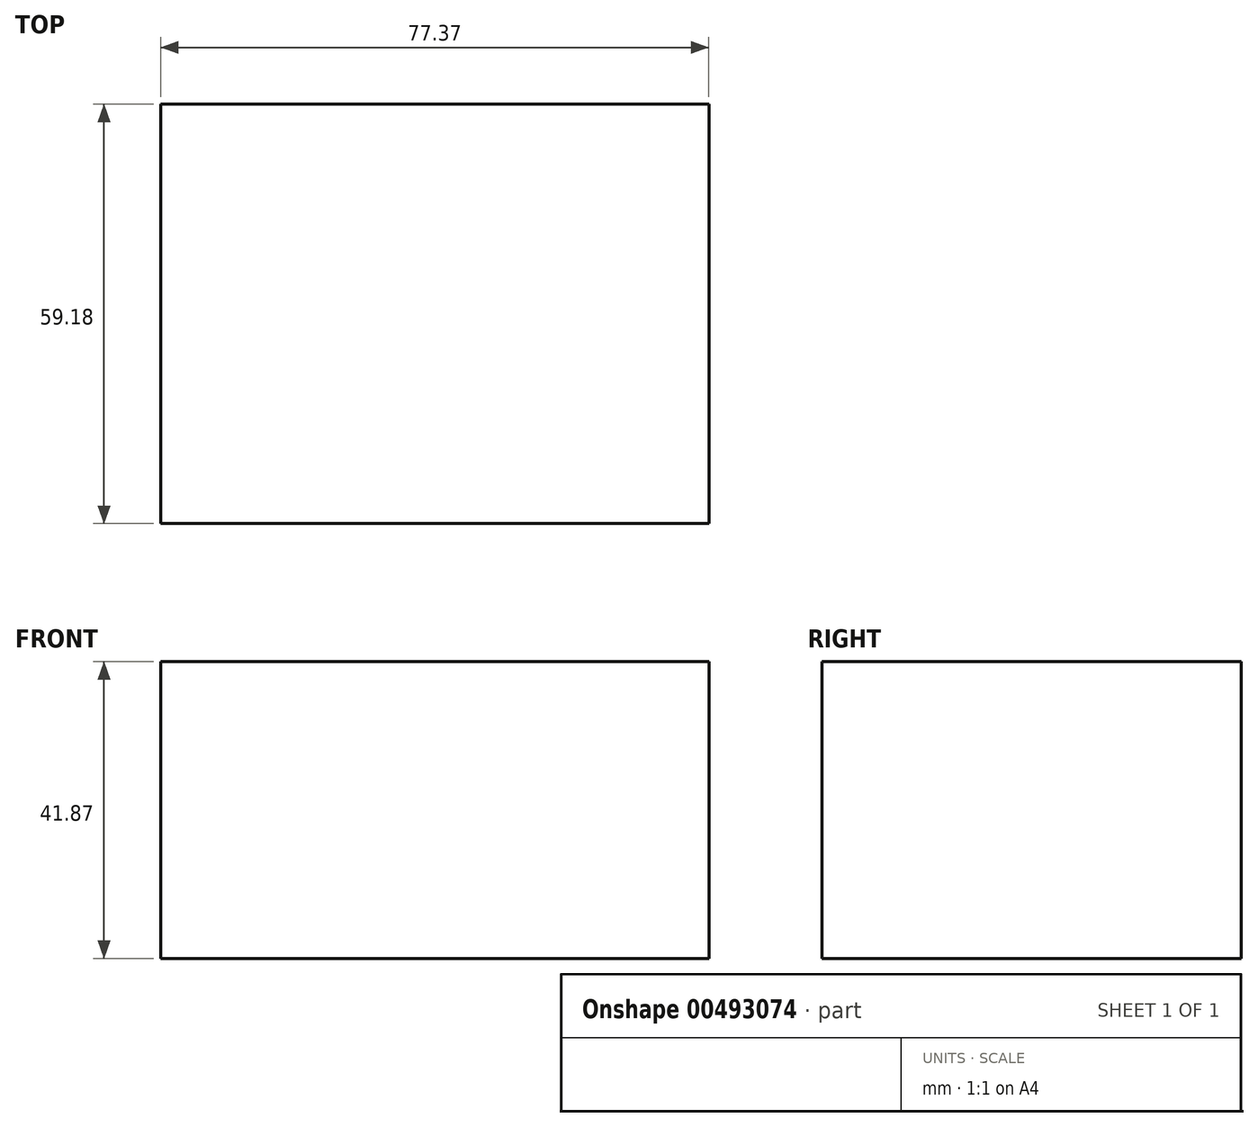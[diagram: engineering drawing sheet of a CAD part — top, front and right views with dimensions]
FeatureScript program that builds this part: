
annotation { "Feature Type Name" : "Feature", "Feature Type Description" : "" }
export const myFeature = defineFeature(function(context is Context, id is Id, definition is map)
    precondition{}
    {
        {
            var Q0;
            Q0=qCreatedBy(makeId("Front.planeOp"),FACE);
            var sketch = newSketch(context, id + "F0", { "sketchPlane" : qUnion([Q0])});
            skLineSegment(sketch, "E0", {"start": v(0, 0) * mm, "end": v(77.37, 0) * mm});
            skLineSegment(sketch, "E1", {"start": v(77.37, 0) * mm, "end": v(77.37, 41.87) * mm});
            skLineSegment(sketch, "E2", {"start": v(77.37, 41.87) * mm, "end": v(0, 41.87) * mm});
            skLineSegment(sketch, "E3", {"start": v(0, 41.87) * mm, "end": v(0, 0) * mm});
            skSolve(sketch);
        }
        {
            var Q0;
            Q0=makeQuery(id+"F0.imprint","IMPRINT",FACE,{"disambiguationData":[TD([[makeQuery(id+"F0.imprint","IMPRINT",EDGE,{"derivedFrom":sQuery(id+"F0.wireOp",EDGE,"E0")}),1.0]])]});
            extrude(context, id + "F1", {"entities" : qUnion([Q0]), "depth" : 59.18 * mm});
        }
    });
